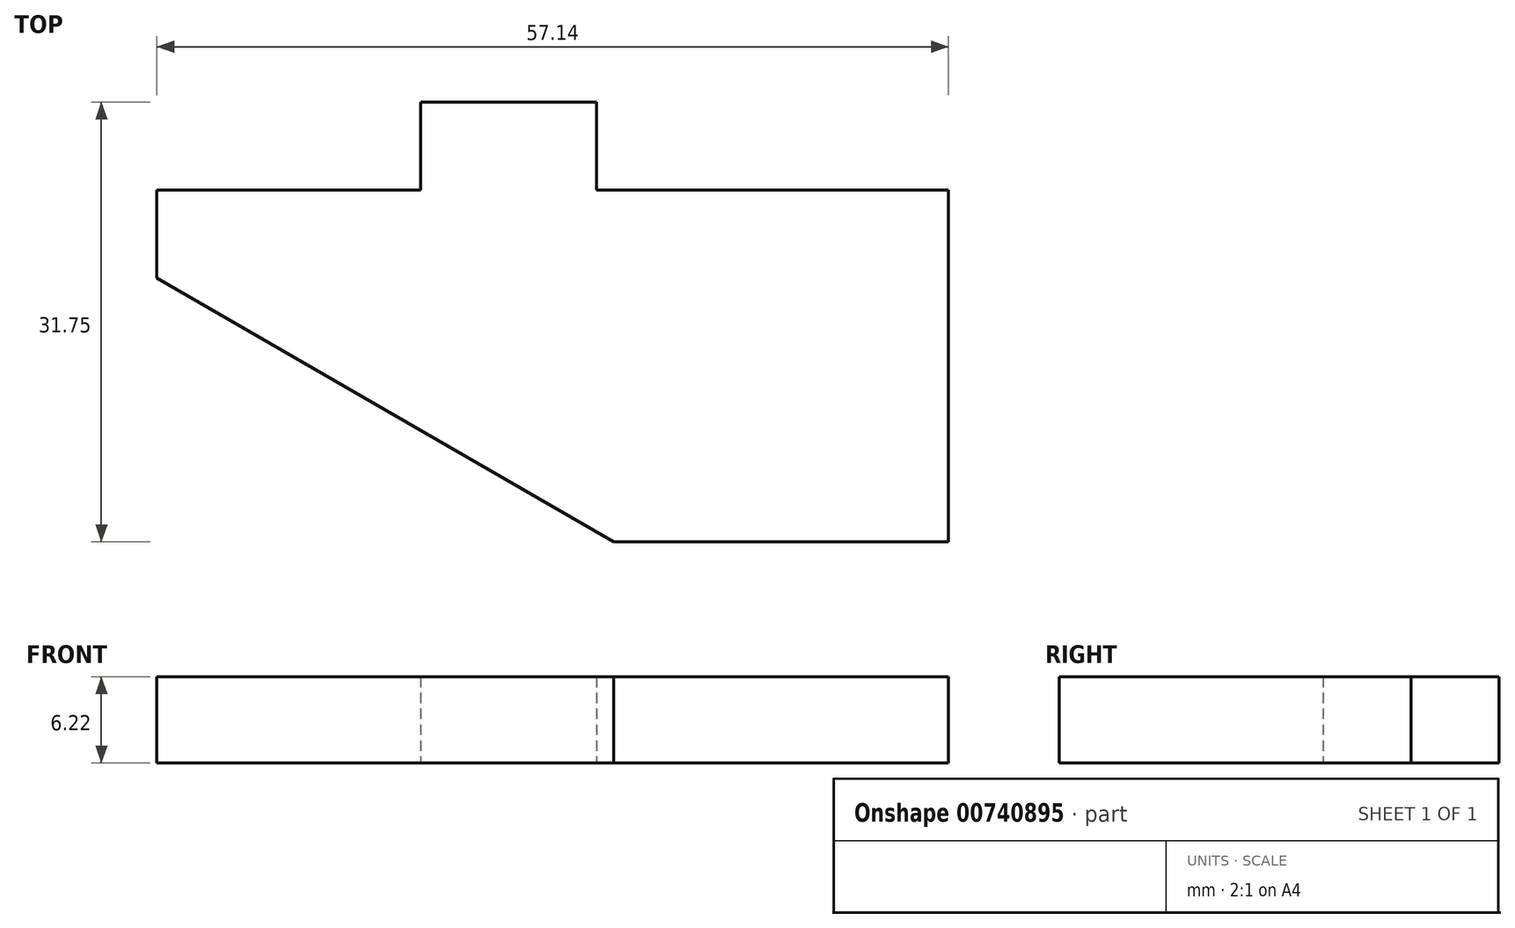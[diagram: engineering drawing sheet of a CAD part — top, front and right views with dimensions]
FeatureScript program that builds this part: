
annotation { "Feature Type Name" : "Feature", "Feature Type Description" : "" }
export const myFeature = defineFeature(function(context is Context, id is Id, definition is map)
    precondition{}
    {
        {
            var Q0;
            Q0=qCreatedBy(makeId("Top.planeOp"),FACE);
            var sketch = newSketch(context, id + "F0", { "sketchPlane" : qUnion([Q0])});
            skLineSegment(sketch, "E0.bottom", {"start": v(28.58, -12.7) * mm, "end": v(-28.58, -12.7) * mm});
            skLineSegment(sketch, "E0.top", {"start": v(28.58, 12.7) * mm, "end": v(-28.58, 12.7) * mm});
            skLineSegment(sketch, "E0.left", {"start": v(28.58, -12.7) * mm, "end": v(28.58, 12.7) * mm});
            skLineSegment(sketch, "E0.right", {"start": v(-28.58, -12.7) * mm, "end": v(-28.58, 12.7) * mm});
            skPoint(sketch, "E0.middle", {"position": v(0, 0) * mm});
            skLineSegment(sketch, "E1.bottom", {"start": v(-9.52, 12.7) * mm, "end": v(3.18, 12.7) * mm});
            skLineSegment(sketch, "E1.top", {"start": v(-9.53, 19.05) * mm, "end": v(3.18, 19.05) * mm});
            skLineSegment(sketch, "E1.left", {"start": v(-9.52, 12.7) * mm, "end": v(-9.53, 19.05) * mm});
            skLineSegment(sketch, "E1.right", {"start": v(3.18, 12.7) * mm, "end": v(3.17, 19.05) * mm});
            skLineSegment(sketch, "E2", {"start": v(4.42, -12.7) * mm, "end": v(-28.58, 6.35) * mm});
            skPoint(sketch, "E3", {"position": v(22.23, 12.7) * mm});
            skSolve(sketch);
        }
        {
            var Q0;
            {var subQ5=sQuery(id+"F0.wireOp",EDGE,"E0.left");Q0=makeQuery(id+"F0.imprint","IMPRINT",FACE,{"disambiguationData":[TD([[makeQuery(id+"F0.imprint","IMPRINT",EDGE,{"derivedFrom":subQ5}),1.0]])]});}
            var Q1;
            Q1=makeQuery(id+"F0.imprint","IMPRINT",FACE,{"disambiguationData":[TD([[makeQuery(id+"F0.imprint","IMPRINT",EDGE,{"derivedFrom":sQuery(id+"F0.wireOp",EDGE,"E1.top")}),-1.0]])]});
            extrude(context, id + "F1", {"entities" : qUnion([Q0, Q1]), "depth" : 6.22 * mm, "offsetDistance" : 25.4 * mm});
        }
    });
